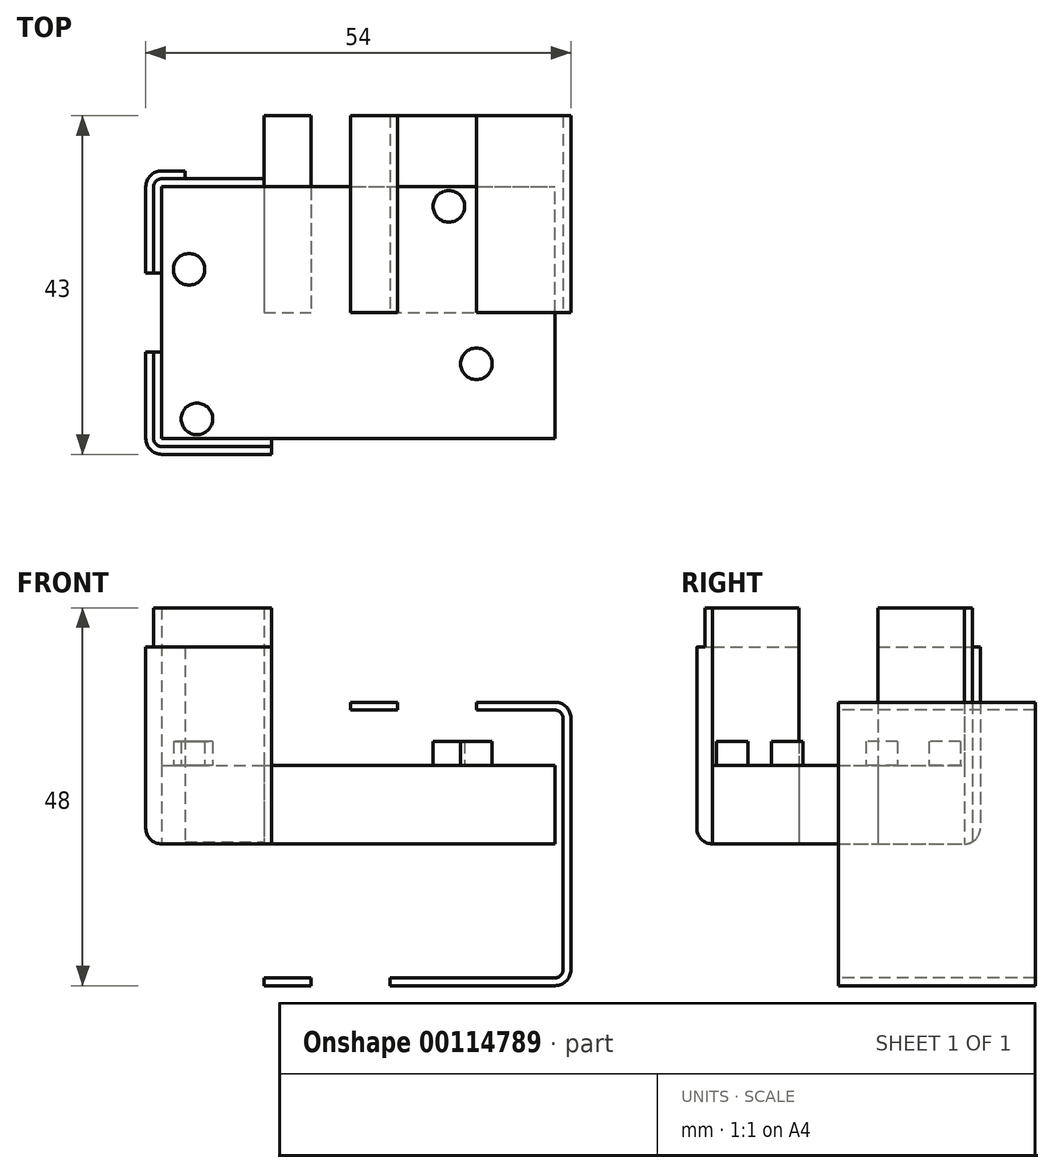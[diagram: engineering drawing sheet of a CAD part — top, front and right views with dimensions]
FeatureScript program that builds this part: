
annotation { "Feature Type Name" : "Feature", "Feature Type Description" : "" }
export const myFeature = defineFeature(function(context is Context, id is Id, definition is map)
    precondition{}
    {
        {
            var Q0;
            Q0=qCreatedBy(makeId("Front.planeOp"),FACE);
            var sketch = newSketch(context, id + "F0", { "sketchPlane" : qUnion([Q0])});
            skPoint(sketch, "E0.middle", {"position": v(0, 0) * mm});
            skLineSegment(sketch, "E1.bottom", {"start": v(-25, 16) * mm, "end": v(25, 16) * mm});
            skLineSegment(sketch, "E1.top", {"start": v(-25, -16) * mm, "end": v(25, -16) * mm});
            skLineSegment(sketch, "E1.left", {"start": v(-25, 16) * mm, "end": v(-25, -16) * mm});
            skLineSegment(sketch, "E1.right", {"start": v(25, 16) * mm, "end": v(25, -16) * mm});
            skLineSegment(sketch, "E2.bottom", {"start": v(-25, 17) * mm, "end": v(25, 17) * mm});
            skLineSegment(sketch, "E2.top", {"start": v(-25, -17) * mm, "end": v(25, -17) * mm});
            skLineSegment(sketch, "E2.left", {"start": v(-26, 16) * mm, "end": v(-26, -16) * mm});
            skLineSegment(sketch, "E2.right", {"start": v(26, 16) * mm, "end": v(26, -16) * mm});
            skLineSegment(sketch, "E3.bottom", {"start": v(25, 18) * mm, "end": v(-25, 18) * mm});
            skLineSegment(sketch, "E3.top", {"start": v(25, -18) * mm, "end": v(-25, -18) * mm});
            skLineSegment(sketch, "E3.left", {"start": v(27, 16) * mm, "end": v(27, -16) * mm});
            skLineSegment(sketch, "E3.right", {"start": v(-27, 16) * mm, "end": v(-27, -16) * mm});
            skLineSegment(sketch, "E4", {"start": v(25, 16) * mm, "end": v(15, 16) * mm});
            skLineSegment(sketch, "E5.bottom", {"start": v(15, 16) * mm, "end": v(5, 16) * mm});
            skLineSegment(sketch, "E5.top", {"start": v(15, 18) * mm, "end": v(5, 18) * mm});
            skLineSegment(sketch, "E5.left", {"start": v(15, 16) * mm, "end": v(15, 18) * mm});
            skLineSegment(sketch, "E5.right", {"start": v(5, 16) * mm, "end": v(5, 18) * mm});
            skLineSegment(sketch, "E6", {"start": v(-25, 16) * mm, "end": v(-25, 5) * mm});
            skLineSegment(sketch, "E7.bottom", {"start": v(-25, 5) * mm, "end": v(-27, 5) * mm});
            skLineSegment(sketch, "E7.top", {"start": v(-25, -5) * mm, "end": v(-27, -5) * mm});
            skLineSegment(sketch, "E7.left", {"start": v(-25, 5) * mm, "end": v(-25, -5) * mm});
            skLineSegment(sketch, "E7.right", {"start": v(-27, 5) * mm, "end": v(-27, -5) * mm});
            skLineSegment(sketch, "E8", {"start": v(-25, -16) * mm, "end": v(-22, -16) * mm});
            skLineSegment(sketch, "E9.bottom", {"start": v(-22, -16) * mm, "end": v(-12, -16) * mm});
            skLineSegment(sketch, "E9.top", {"start": v(-22, -18) * mm, "end": v(-12, -18) * mm});
            skLineSegment(sketch, "E9.left", {"start": v(-22, -16) * mm, "end": v(-22, -18) * mm});
            skLineSegment(sketch, "E9.right", {"start": v(-12, -16) * mm, "end": v(-12, -18) * mm});
            skLineSegment(sketch, "E10", {"start": v(-12, -16) * mm, "end": v(-6, -16) * mm});
            skLineSegment(sketch, "E11.bottom", {"start": v(-6, -16) * mm, "end": v(4, -16) * mm});
            skLineSegment(sketch, "E11.top", {"start": v(-6, -18) * mm, "end": v(4, -18) * mm});
            skLineSegment(sketch, "E11.left", {"start": v(-6, -16) * mm, "end": v(-6, -18) * mm});
            skLineSegment(sketch, "E11.right", {"start": v(4, -16) * mm, "end": v(4, -18) * mm});
            skLineSegment(sketch, "E12", {"start": v(5, 16) * mm, "end": v(-1, 16) * mm});
            skLineSegment(sketch, "E13.bottom", {"start": v(-1, 16) * mm, "end": v(-11, 16) * mm});
            skLineSegment(sketch, "E13.top", {"start": v(-1, 18) * mm, "end": v(-11, 18) * mm});
            skLineSegment(sketch, "E13.left", {"start": v(-1, 16) * mm, "end": v(-1, 18) * mm});
            skLineSegment(sketch, "E13.right", {"start": v(-11, 16) * mm, "end": v(-11, 18) * mm});
            skPoint(sketch, "E14.visualSharp", {"position": v(26, 17) * mm});
            skArc(sketch, "E14.filletArc", {"start": v(26, 16) * mm, "mid": v(25.7, 16.7) * mm, "end": v(25, 17) * mm});
            skPoint(sketch, "E15.visualSharp", {"position": v(-26, 17) * mm});
            skArc(sketch, "E15.filletArc", {"start": v(-25, 17) * mm, "mid": v(-25.7, 16.7) * mm, "end": v(-26, 16) * mm});
            skPoint(sketch, "E16.visualSharp", {"position": v(-26, -17) * mm});
            skArc(sketch, "E16.filletArc", {"start": v(-26, -16) * mm, "mid": v(-25.7, -16.7) * mm, "end": v(-25, -17) * mm});
            skPoint(sketch, "E17.visualSharp", {"position": v(26, -17) * mm});
            skArc(sketch, "E17.filletArc", {"start": v(25, -17) * mm, "mid": v(25.7, -16.7) * mm, "end": v(26, -16) * mm});
            skPoint(sketch, "E18.visualSharp", {"position": v(27, 18) * mm});
            skArc(sketch, "E18.filletArc", {"start": v(27, 16) * mm, "mid": v(26.41, 17.41) * mm, "end": v(25, 18) * mm});
            skPoint(sketch, "E19.visualSharp", {"position": v(-27, 18) * mm});
            skArc(sketch, "E19.filletArc", {"start": v(-25, 18) * mm, "mid": v(-26.41, 17.41) * mm, "end": v(-27, 16) * mm});
            skPoint(sketch, "E20.visualSharp", {"position": v(-27, -18) * mm});
            skArc(sketch, "E20.filletArc", {"start": v(-27, -16) * mm, "mid": v(-26.41, -17.41) * mm, "end": v(-25, -18) * mm});
            skPoint(sketch, "E21.visualSharp", {"position": v(27, -18) * mm});
            skArc(sketch, "E21.filletArc", {"start": v(25, -18) * mm, "mid": v(26.41, -17.41) * mm, "end": v(27, -16) * mm});
            skLineSegment(sketch, "E22.bottom", {"start": v(25, -16) * mm, "end": v(11.5, -16) * mm});
            skLineSegment(sketch, "E22.left", {"start": v(25, -16) * mm, "end": v(25, -13.5) * mm});
            skLineSegment(sketch, "E22.right", {"start": v(11.5, -16) * mm, "end": v(11.5, -13.5) * mm});
            skLineSegment(sketch, "E23.left", {"start": v(25, 16) * mm, "end": v(25, 6.5) * mm});
            skLineSegment(sketch, "E23.right", {"start": v(15, 16) * mm, "end": v(15, 6.5) * mm});
            skLineSegment(sketch, "E24.bottom", {"start": v(-25, 16) * mm, "end": v(-20.5, 16) * mm});
            skLineSegment(sketch, "E24.left", {"start": v(-25, 16) * mm, "end": v(-25, 13.5) * mm});
            skLineSegment(sketch, "E24.right", {"start": v(-20.5, 16) * mm, "end": v(-20.5, 13.5) * mm});
            skLineSegment(sketch, "E25.bottom", {"start": v(-25, -16) * mm, "end": v(-21.5, -16) * mm});
            skLineSegment(sketch, "E25.left", {"start": v(-25, -16) * mm, "end": v(-25, -5.5) * mm});
            skLineSegment(sketch, "E25.right", {"start": v(-21.5, -16) * mm, "end": v(-21.5, -5.5) * mm});
            skCircle(sketch, "E26", {"center": v(15, 6.5) * mm, "radius": 2 * mm});
            skCircle(sketch, "E27", {"center": v(-21.5, -5.5) * mm, "radius": 2 * mm});
            skCircle(sketch, "E28", {"center": v(11.5, -13.5) * mm, "radius": 2 * mm});
            skCircle(sketch, "E29", {"center": v(-20.5, 13.5) * mm, "radius": 2 * mm});
            skLineSegment(sketch, "E30", {"start": v(0, 0) * mm, "end": v(15.4, 0) * mm});
            skSolve(sketch);
        }
        {
            var Q0;
            Q0=makeQuery(id+"F0.imprint","IMPRINT",FACE,{"disambiguationData":[TD([[makeQuery(id+"F0.imprint","IMPRINT",EDGE,{"derivedFrom":sQuery(id+"F0.wireOp",EDGE,"E1.bottom")}),-1.0]])]});
            var Q1;
            {var subQ5=sQuery(id+"F0.wireOp",EDGE,"E13.bottom");Q1=makeQuery(id+"F0.imprint","IMPRINT",FACE,{"disambiguationData":[TD([[makeQuery(id+"F0.imprint","IMPRINT",EDGE,{"derivedFrom":subQ5}),-1.0]])]});}
            var Q2;
            {var subQ5=sQuery(id+"F0.wireOp",EDGE,"E13.top");Q2=makeQuery(id+"F0.imprint","IMPRINT",FACE,{"disambiguationData":[TD([[makeQuery(id+"F0.imprint","IMPRINT",EDGE,{"derivedFrom":subQ5}),1.0]])]});}
            var Q3;
            {var subQ5=sQuery(id+"F0.wireOp",EDGE,"E5.bottom");Q3=makeQuery(id+"F0.imprint","IMPRINT",FACE,{"disambiguationData":[TD([[makeQuery(id+"F0.imprint","IMPRINT",EDGE,{"derivedFrom":subQ5}),-1.0]])]});}
            var Q4;
            {var subQ5=sQuery(id+"F0.wireOp",EDGE,"E5.top");Q4=makeQuery(id+"F0.imprint","IMPRINT",FACE,{"disambiguationData":[TD([[makeQuery(id+"F0.imprint","IMPRINT",EDGE,{"derivedFrom":subQ5}),1.0]])]});}
            var Q5;
            {var subQ5=sQuery(id+"F0.wireOp",EDGE,"E11.top");Q5=makeQuery(id+"F0.imprint","IMPRINT",FACE,{"disambiguationData":[TD([[makeQuery(id+"F0.imprint","IMPRINT",EDGE,{"derivedFrom":subQ5}),1.0]])]});}
            var Q6;
            {var subQ5=sQuery(id+"F0.wireOp",EDGE,"E11.bottom");Q6=makeQuery(id+"F0.imprint","IMPRINT",FACE,{"disambiguationData":[TD([[makeQuery(id+"F0.imprint","IMPRINT",EDGE,{"derivedFrom":subQ5}),-1.0]])]});}
            var Q7;
            {var subQ1=sQuery(id+"F0.wireOp",EDGE,"E9.bottom");Q7=makeQuery(id+"F0.imprint","IMPRINT",FACE,{"disambiguationData":[TD([[makeQuery(id+"F0.imprint","IMPRINT",EDGE,{"derivedFrom":subQ1}),-1.0]])]});}
            var Q8;
            {var subQ5=sQuery(id+"F0.wireOp",EDGE,"E9.top");Q8=makeQuery(id+"F0.imprint","IMPRINT",FACE,{"disambiguationData":[TD([[makeQuery(id+"F0.imprint","IMPRINT",EDGE,{"derivedFrom":subQ5}),1.0]])]});}
            var Q9;
            {var subQ5=sQuery(id+"F0.wireOp",EDGE,"E7.right");Q9=makeQuery(id+"F0.imprint","IMPRINT",FACE,{"disambiguationData":[TD([[makeQuery(id+"F0.imprint","IMPRINT",EDGE,{"derivedFrom":subQ5}),1.0]])]});}
            var Q10;
            {var subQ5=sQuery(id+"F0.wireOp",EDGE,"E7.left");Q10=makeQuery(id+"F0.imprint","IMPRINT",FACE,{"disambiguationData":[TD([[makeQuery(id+"F0.imprint","IMPRINT",EDGE,{"derivedFrom":subQ5}),-1.0]])]});}
            extrude(context, id + "F1", {"entities" : qUnion([Q0, Q1, Q2, Q3, Q4, Q5, Q6, Q7, Q8, Q9, Q10]), "oppositeDirection" : true, "depth" : 10 * mm});
        }
        {
            var Q0;
            {var subQ0=sQuery(id+"F0.wireOp",EDGE,"E24.right");Q0=makeQuery(id+"F0.imprint","IMPRINT",FACE,{"disambiguationData":[TD([[makeQuery(id+"F0.imprint","IMPRINT",EDGE,{"derivedFrom":subQ0}),1.0]])]});}
            var Q1;
            {var subQ0=sQuery(id+"F0.wireOp",EDGE,"E24.right");Q1=makeQuery(id+"F0.imprint","IMPRINT",FACE,{"disambiguationData":[TD([[makeQuery(id+"F0.imprint","IMPRINT",EDGE,{"derivedFrom":subQ0}),-1.0]])]});}
            var Q2;
            {var subQ0=sQuery(id+"F0.wireOp",EDGE,"E25.right");var subQ1=sQuery(id+"F0.wireOp",EDGE,"E25.top");var subQ2=makeQuery(id+"F0.imprint","INTERSECT",VERTEX,{"derivedFrom":[subQ1,subQ0]});Q2=makeQuery(id+"F0.imprint","IMPRINT",FACE,{"disambiguationData":[TD([[makeQuery(id+"F0.imprint","IMPRINT",EDGE,{"disambiguationData":[TD([[subQ2,1.0]])],"derivedFrom":subQ1}),1.0]])]});}
            var Q3;
            {var subQ0=sQuery(id+"F0.wireOp",EDGE,"E25.right");var subQ1=sQuery(id+"F0.wireOp",EDGE,"E25.top");var subQ2=makeQuery(id+"F0.imprint","INTERSECT",VERTEX,{"derivedFrom":[subQ1,subQ0]});Q3=makeQuery(id+"F0.imprint","IMPRINT",FACE,{"disambiguationData":[TD([[makeQuery(id+"F0.imprint","IMPRINT",EDGE,{"disambiguationData":[TD([[subQ2,1.0]])],"derivedFrom":subQ1}),-1.0]])]});}
            var Q4;
            {var subQ0=sQuery(id+"F0.wireOp",EDGE,"E23.right");var subQ1=sQuery(id+"F0.wireOp",EDGE,"E23.top");var subQ2=makeQuery(id+"F0.imprint","INTERSECT",VERTEX,{"derivedFrom":[subQ1,subQ0]});Q4=makeQuery(id+"F0.imprint","IMPRINT",FACE,{"disambiguationData":[TD([[makeQuery(id+"F0.imprint","IMPRINT",EDGE,{"disambiguationData":[TD([[subQ2,1.0]])],"derivedFrom":subQ1}),1.0]])]});}
            var Q5;
            {var subQ0=sQuery(id+"F0.wireOp",EDGE,"E23.right");var subQ1=sQuery(id+"F0.wireOp",EDGE,"E23.top");var subQ2=makeQuery(id+"F0.imprint","INTERSECT",VERTEX,{"derivedFrom":[subQ1,subQ0]});Q5=makeQuery(id+"F0.imprint","IMPRINT",FACE,{"disambiguationData":[TD([[makeQuery(id+"F0.imprint","IMPRINT",EDGE,{"disambiguationData":[TD([[subQ2,1.0]])],"derivedFrom":subQ1}),-1.0]])]});}
            var Q6;
            {var subQ0=sQuery(id+"F0.wireOp",EDGE,"E22.right");Q6=makeQuery(id+"F0.imprint","IMPRINT",FACE,{"disambiguationData":[TD([[makeQuery(id+"F0.imprint","IMPRINT",EDGE,{"derivedFrom":subQ0}),1.0]])]});}
            var Q7;
            {var subQ0=sQuery(id+"F0.wireOp",EDGE,"E22.right");Q7=makeQuery(id+"F0.imprint","IMPRINT",FACE,{"disambiguationData":[TD([[makeQuery(id+"F0.imprint","IMPRINT",EDGE,{"derivedFrom":subQ0}),-1.0]])]});}
            var Q8;
            Q8=makeQuery(id+"F0.imprint","IMPRINT",FACE,{"disambiguationData":[TD([[makeQuery(id+"F0.imprint","IMPRINT",EDGE,{"derivedFrom":sQuery(id+"F0.wireOp",EDGE,"E29")}),1.0]])]});
            var Q9;
            Q9=makeQuery(id+"F0.imprint","IMPRINT",FACE,{"disambiguationData":[TD([[makeQuery(id+"F0.imprint","IMPRINT",EDGE,{"derivedFrom":sQuery(id+"F0.wireOp",EDGE,"E27")}),1.0]])]});
            var Q10;
            Q10=makeQuery(id+"F0.imprint","IMPRINT",FACE,{"disambiguationData":[TD([[makeQuery(id+"F0.imprint","IMPRINT",EDGE,{"derivedFrom":sQuery(id+"F0.wireOp",EDGE,"E28")}),1.0]])]});
            var Q11;
            Q11=makeQuery(id+"F0.imprint","IMPRINT",FACE,{"disambiguationData":[TD([[makeQuery(id+"F0.imprint","IMPRINT",EDGE,{"derivedFrom":sQuery(id+"F0.wireOp",EDGE,"E26")}),1.0]])]});
            var Q12;
            Q12=sQuery(id+"F0.wireOp",EDGE,"vqUXj9zX-bHck-LdTY-wkr8-7sMtbMIrG8t5");
            var Q13;
            Q13=sQuery(id+"F0.wireOp",EDGE,"DzZTjJkk-xPD1-vqrs-CiXM-9Zj7VaGM5017");
            extrude(context, id + "F2", {"entities" : qUnion([Q0, Q1, Q2, Q3, Q4, Q5, Q6, Q7, Q8, Q9, Q10, Q11]), "operationType" : NewBodyOperationType.ADD, "surfaceEntities" : qUnion([Q12, Q13]), "oppositeDirection" : true, "depth" : 13 * mm});
        }
        {
            var Q0;
            {var subQ11=sQuery(id+"F0.wireOp",EDGE,"E1.top");Q0=makeQuery(id+"F0.imprint","IMPRINT",FACE,{"disambiguationData":[TD([[makeQuery(id+"F0.imprint","IMPRINT",EDGE,{"derivedFrom":subQ11}),-1.0]])]});}
            var Q1;
            {var subQ5=sQuery(id+"F0.wireOp",EDGE,"E12");Q1=makeQuery(id+"F0.imprint","IMPRINT",FACE,{"disambiguationData":[TD([[makeQuery(id+"F0.imprint","IMPRINT",EDGE,{"derivedFrom":subQ5}),-1.0]])]});}
            var Q2;
            {var subQ8=sQuery(id+"F0.wireOp",EDGE,"E1.bottom");Q2=makeQuery(id+"F0.imprint","IMPRINT",FACE,{"disambiguationData":[TD([[makeQuery(id+"F0.imprint","IMPRINT",EDGE,{"derivedFrom":subQ8}),1.0]])]});}
            var Q3;
            {var subQ1=sQuery(id+"F0.wireOp",EDGE,"E1.left");Q3=makeQuery(id+"F0.imprint","IMPRINT",FACE,{"disambiguationData":[TD([[makeQuery(id+"F0.imprint","IMPRINT",EDGE,{"derivedFrom":subQ1}),-1.0]])]});}
            var Q4;
            {var subQ5=sQuery(id+"F0.wireOp",EDGE,"E10");Q4=makeQuery(id+"F0.imprint","IMPRINT",FACE,{"disambiguationData":[TD([[makeQuery(id+"F0.imprint","IMPRINT",EDGE,{"derivedFrom":subQ5}),-1.0]])]});}
            extrude(context, id + "F3", {"entities" : qUnion([Q0, Q1, Q2, Q3, Q4]), "operationType" : NewBodyOperationType.ADD, "oppositeDirection" : true, "depth" : 30 * mm});
        }
        {
            var Q0;
            {var subQ0=sQuery(id+"F0.wireOp",EDGE,"E13.left");var subQ1=sQuery(id+"F0.wireOp",EDGE,"E2.bottom");var subQ2=makeQuery(id+"F0.imprint","INTERSECT",VERTEX,{"derivedFrom":[subQ1,subQ0]});Q0=makeQuery(id+"F0.imprint","IMPRINT",FACE,{"disambiguationData":[TD([[makeQuery(id+"F0.imprint","IMPRINT",EDGE,{"disambiguationData":[TD([[subQ2,-1.0]])],"derivedFrom":subQ1}),1.0]])]});}
            var Q1;
            Q1=makeQuery(id+"F0.imprint","IMPRINT",FACE,{"disambiguationData":[TD([[makeQuery(id+"F0.imprint","IMPRINT",EDGE,{"derivedFrom":sQuery(id+"F0.wireOp",EDGE,"E2.right")}),1.0]])]});
            var Q2;
            {var subQ4=sQuery(id+"F0.wireOp",EDGE,"E15.filletArc");Q2=makeQuery(id+"F0.imprint","IMPRINT",FACE,{"disambiguationData":[TD([[makeQuery(id+"F0.imprint","IMPRINT",EDGE,{"derivedFrom":subQ4}),-1.0]])]});}
            var Q3;
            {var subQ4=sQuery(id+"F0.wireOp",EDGE,"E16.filletArc");Q3=makeQuery(id+"F0.imprint","IMPRINT",FACE,{"disambiguationData":[TD([[makeQuery(id+"F0.imprint","IMPRINT",EDGE,{"derivedFrom":subQ4}),-1.0]])]});}
            var Q4;
            {var subQ0=sQuery(id+"F0.wireOp",EDGE,"E9.right");var subQ1=sQuery(id+"F0.wireOp",EDGE,"E2.top");var subQ2=makeQuery(id+"F0.imprint","INTERSECT",VERTEX,{"derivedFrom":[subQ1,subQ0]});Q4=makeQuery(id+"F0.imprint","IMPRINT",FACE,{"disambiguationData":[TD([[makeQuery(id+"F0.imprint","IMPRINT",EDGE,{"disambiguationData":[TD([[subQ2,-1.0]])],"derivedFrom":subQ1}),-1.0]])]});}
            extrude(context, id + "F4", {"entities" : qUnion([Q0, Q1, Q2, Q3, Q4]), "operationType" : NewBodyOperationType.ADD, "oppositeDirection" : true, "depth" : 25 * mm});
        }
        {
            var Q0;
            {var subQ0=sQuery(id+"F0.wireOp",EDGE,"E3.bottom");var subQ1=sQuery(id+"F0.wireOp",EDGE,"E13.top");var subQ2=sQuery(id+"F0.wireOp",EDGE,"E5.top");Q0=makeQuery(id+"F4.boolean.opBoolean","MERGE",EDGE,{"derivedFrom":[makeQuery(id+"F1.opExtrude","CAP_EDGE",EDGE,{"disambiguationData":[OSD([subQ2])],"isStart":true}),makeQuery(id+"F1.opExtrude","CAP_EDGE",EDGE,{"disambiguationData":[OSD([subQ1])],"isStart":true}),makeQuery(id+"F4.opExtrude","CAP_EDGE",EDGE,{"disambiguationData":[OSD([subQ0]),TDD([makeQuery(id+"F0.imprint","IMPRINT",EDGE,{"disambiguationData":[TD([[makeQuery(id+"F0.imprint","INTERSECT",VERTEX,{"derivedFrom":[subQ0,sQuery(id+"F0.wireOp",EDGE,"E18.filletArc")]}),-1.0]])],"derivedFrom":subQ0})])],"isStart":true}),makeQuery(id+"F4.opExtrude","CAP_EDGE",EDGE,{"disambiguationData":[OSD([subQ0]),TDD([makeQuery(id+"F0.imprint","IMPRINT",EDGE,{"disambiguationData":[TD([[makeQuery(id+"F0.imprint","INTERSECT",VERTEX,{"derivedFrom":[subQ0,subQ2,sQuery(id+"F0.wireOp",EDGE,"E5.right")]}),-1.0]])],"derivedFrom":subQ0})])],"isStart":true}),makeQuery(id+"F4.opExtrude","CAP_EDGE",EDGE,{"disambiguationData":[OSD([subQ0]),TDD([makeQuery(id+"F0.imprint","IMPRINT",EDGE,{"disambiguationData":[TD([[makeQuery(id+"F0.imprint","INTERSECT",VERTEX,{"derivedFrom":[subQ0,sQuery(id+"F0.wireOp",EDGE,"E19.filletArc")]}),1.0]])],"derivedFrom":subQ0})])],"isStart":true})]});}
            var Q1;
            Q1=makeQuery(id+"F4.opExtrude","CAP_EDGE",EDGE,{"disambiguationData":[OSD([sQuery(id+"F0.wireOp",EDGE,"E19.filletArc")])],"isStart":true});
            var Q2;
            {var subQ0=sQuery(id+"F0.wireOp",EDGE,"E3.right");var subQ1=sQuery(id+"F0.wireOp",EDGE,"E7.right");Q2=makeQuery(id+"F4.boolean.opBoolean","MERGE",EDGE,{"derivedFrom":[makeQuery(id+"F1.opExtrude","CAP_EDGE",EDGE,{"disambiguationData":[OSD([subQ1])],"isStart":true}),makeQuery(id+"F4.opExtrude","CAP_EDGE",EDGE,{"disambiguationData":[OSD([subQ0]),TDD([makeQuery(id+"F0.imprint","IMPRINT",EDGE,{"disambiguationData":[TD([[makeQuery(id+"F0.imprint","INTERSECT",VERTEX,{"derivedFrom":[subQ0,sQuery(id+"F0.wireOp",EDGE,"E19.filletArc")]}),-1.0]])],"derivedFrom":subQ0})])],"isStart":true}),makeQuery(id+"F4.opExtrude","CAP_EDGE",EDGE,{"disambiguationData":[OSD([subQ0]),TDD([makeQuery(id+"F0.imprint","IMPRINT",EDGE,{"disambiguationData":[TD([[makeQuery(id+"F0.imprint","INTERSECT",VERTEX,{"derivedFrom":[subQ0,sQuery(id+"F0.wireOp",EDGE,"E20.filletArc")]}),1.0]])],"derivedFrom":subQ0})])],"isStart":true})]});}
            var Q3;
            Q3=makeQuery(id+"F4.opExtrude","CAP_EDGE",EDGE,{"disambiguationData":[OSD([sQuery(id+"F0.wireOp",EDGE,"E20.filletArc")])],"isStart":true});
            var Q4;
            {var subQ0=sQuery(id+"F0.wireOp",EDGE,"E3.top");var subQ1=sQuery(id+"F0.wireOp",EDGE,"E9.top");var subQ2=sQuery(id+"F0.wireOp",EDGE,"E11.top");Q4=makeQuery(id+"F4.boolean.opBoolean","MERGE",EDGE,{"derivedFrom":[makeQuery(id+"F1.opExtrude","CAP_EDGE",EDGE,{"disambiguationData":[OSD([subQ1])],"isStart":true}),makeQuery(id+"F1.opExtrude","CAP_EDGE",EDGE,{"disambiguationData":[OSD([subQ2])],"isStart":true}),makeQuery(id+"F4.opExtrude","CAP_EDGE",EDGE,{"disambiguationData":[OSD([subQ0]),TDD([makeQuery(id+"F0.imprint","IMPRINT",EDGE,{"disambiguationData":[TD([[makeQuery(id+"F0.imprint","INTERSECT",VERTEX,{"derivedFrom":[subQ0,sQuery(id+"F0.wireOp",EDGE,"E21.filletArc")]}),-1.0]])],"derivedFrom":subQ0})])],"isStart":true}),makeQuery(id+"F4.opExtrude","CAP_EDGE",EDGE,{"disambiguationData":[OSD([subQ0]),TDD([makeQuery(id+"F0.imprint","IMPRINT",EDGE,{"disambiguationData":[TD([[makeQuery(id+"F0.imprint","INTERSECT",VERTEX,{"derivedFrom":[subQ0,subQ1,sQuery(id+"F0.wireOp",EDGE,"E9.right")]}),1.0]])],"derivedFrom":subQ0})])],"isStart":true}),makeQuery(id+"F4.opExtrude","CAP_EDGE",EDGE,{"disambiguationData":[OSD([subQ0]),TDD([makeQuery(id+"F0.imprint","IMPRINT",EDGE,{"disambiguationData":[TD([[makeQuery(id+"F0.imprint","INTERSECT",VERTEX,{"derivedFrom":[subQ0,sQuery(id+"F0.wireOp",EDGE,"E20.filletArc")]}),1.0]])],"derivedFrom":subQ0})])],"isStart":true})]});}
            var Q5;
            Q5=makeQuery(id+"F4.opExtrude","CAP_EDGE",EDGE,{"disambiguationData":[OSD([sQuery(id+"F0.wireOp",EDGE,"E21.filletArc")])],"isStart":true});
            var Q6;
            Q6=makeQuery(id+"F4.opExtrude","CAP_EDGE",EDGE,{"disambiguationData":[OSD([sQuery(id+"F0.wireOp",EDGE,"E3.left")])],"isStart":true});
            var Q7;
            Q7=makeQuery(id+"F4.opExtrude","CAP_EDGE",EDGE,{"disambiguationData":[OSD([sQuery(id+"F0.wireOp",EDGE,"E18.filletArc")])],"isStart":true});
            fillet(context, id + "F5", {"entities" : qUnion([Q0, Q1, Q2, Q3, Q4, Q5, Q6, Q7]), "radius" : 2 * mm, "tangentPropagation" : true, "allowEdgeOverflow" : false});
        }
        {
            var Q0;
            Q0=makeQuery(id+"F1.opExtrude","SWEPT_BODY",BODY,{"disambiguationData":[OSD([sQuery(id+"F0.wireOp",EDGE,"E1.bottom"),sQuery(id+"F0.wireOp",EDGE,"E1.top"),sQuery(id+"F0.wireOp",EDGE,"E1.left"),sQuery(id+"F0.wireOp",EDGE,"E1.right"),sQuery(id+"F0.wireOp",EDGE,"E5.top"),sQuery(id+"F0.wireOp",EDGE,"E5.left"),sQuery(id+"F0.wireOp",EDGE,"E5.right"),sQuery(id+"F0.wireOp",EDGE,"E6"),sQuery(id+"F0.wireOp",EDGE,"E7.bottom"),sQuery(id+"F0.wireOp",EDGE,"E7.top"),sQuery(id+"F0.wireOp",EDGE,"E7.right"),sQuery(id+"F0.wireOp",EDGE,"E9.top"),sQuery(id+"F0.wireOp",EDGE,"E9.left"),sQuery(id+"F0.wireOp",EDGE,"E9.right"),sQuery(id+"F0.wireOp",EDGE,"E10"),sQuery(id+"F0.wireOp",EDGE,"E11.top"),sQuery(id+"F0.wireOp",EDGE,"E11.left"),sQuery(id+"F0.wireOp",EDGE,"E11.right"),sQuery(id+"F0.wireOp",EDGE,"E12"),sQuery(id+"F0.wireOp",EDGE,"E13.top"),sQuery(id+"F0.wireOp",EDGE,"E13.left"),sQuery(id+"F0.wireOp",EDGE,"E13.right"),sQuery(id+"F0.wireOp",EDGE,"E22.bottom"),sQuery(id+"F0.wireOp",EDGE,"E22.left"),sQuery(id+"F0.wireOp",EDGE,"E4"),sQuery(id+"F0.wireOp",EDGE,"E23.left"),sQuery(id+"F0.wireOp",EDGE,"E24.bottom"),sQuery(id+"F0.wireOp",EDGE,"E24.left"),sQuery(id+"F0.wireOp",EDGE,"E25.bottom"),sQuery(id+"F0.wireOp",EDGE,"E25.left"),sQuery(id+"F0.wireOp",EDGE,"E26"),sQuery(id+"F0.wireOp",EDGE,"E27"),sQuery(id+"F0.wireOp",EDGE,"E28"),sQuery(id+"F0.wireOp",EDGE,"E29")])]});
            var Q1;
            Q1=sQuery(id+"F0.wireOp",EDGE,"E30");
            transform(context, id + "F6", {"entities" : qUnion([Q0]), "transformType" : TransformType.ROTATION, "transformAxis" : qUnion([Q1]), "angle" : 90 * degree, "makeCopy" : false});
        }
    });
